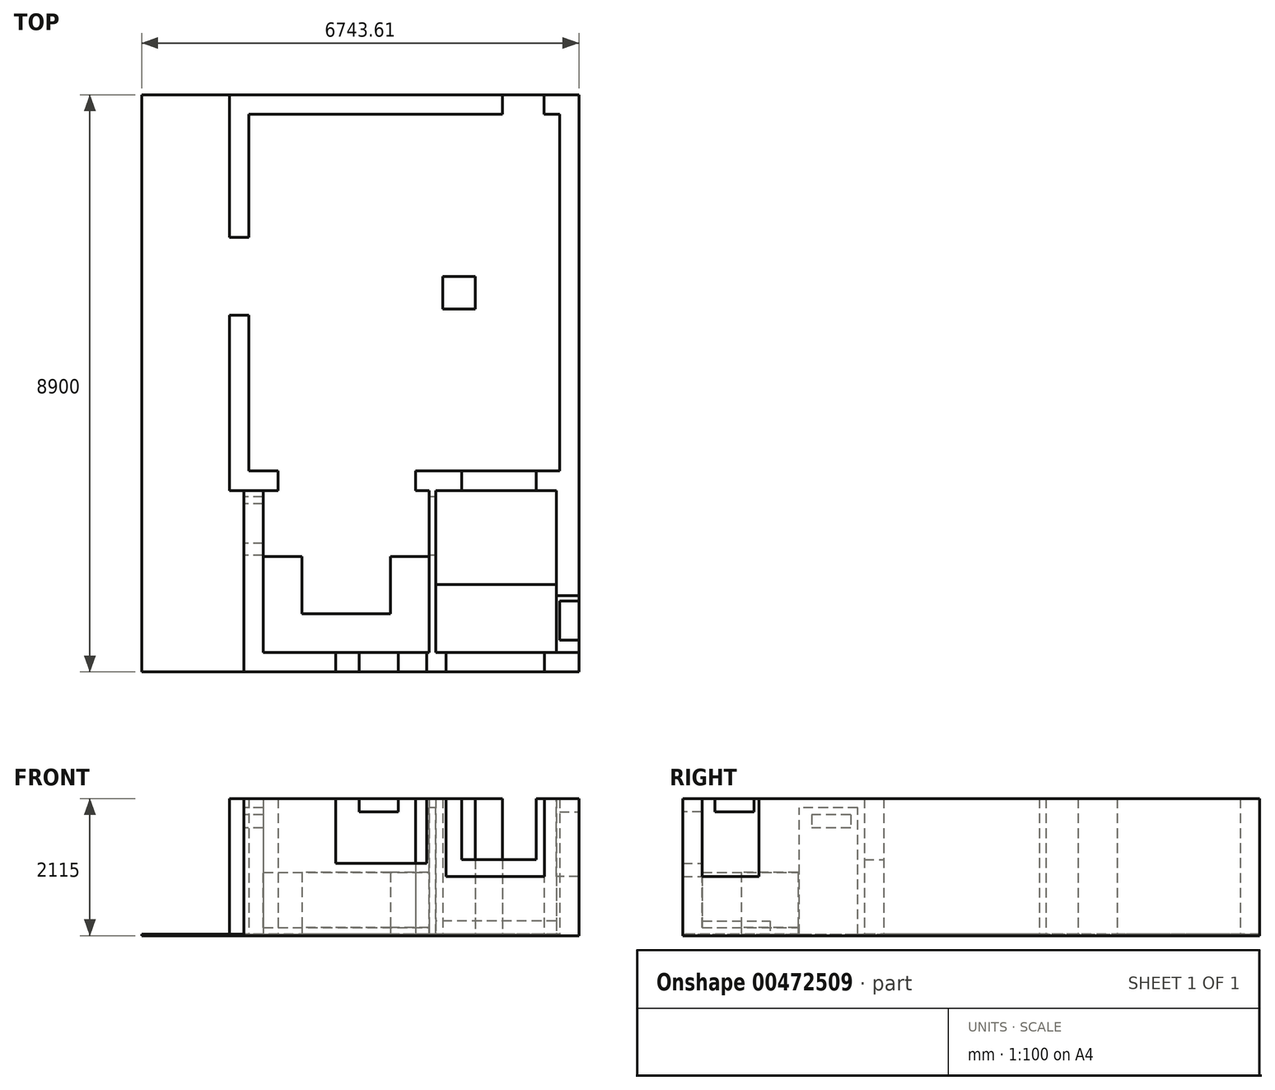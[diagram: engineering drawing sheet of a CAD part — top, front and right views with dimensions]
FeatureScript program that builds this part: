
annotation { "Feature Type Name" : "Feature", "Feature Type Description" : "" }
export const myFeature = defineFeature(function(context is Context, id is Id, definition is map)
    precondition{}
    {
        {
            var Q0;
            Q0=qCreatedBy(makeId("Top.planeOp"),FACE);
            var sketch = newSketch(context, id + "F0", { "sketchPlane" : qUnion([Q0])});
            skLineSegment(sketch, "E0", {"start": v(-2549.23, -2913.2) * mm, "end": v(-2549.23, -513.2) * mm});
            skLineSegment(sketch, "E1", {"start": v(-2549.23, -513.2) * mm, "end": v(-2549.23, 686.8) * mm});
            skLineSegment(sketch, "E2", {"start": v(-2549.23, 686.8) * mm, "end": v(-2549.23, 2586.8) * mm});
            skLineSegment(sketch, "E3", {"start": v(-2549.23, 2586.8) * mm, "end": v(1357.86, 2586.8) * mm});
            skLineSegment(sketch, "E4", {"start": v(1357.86, 2586.8) * mm, "end": v(1999.13, 2586.8) * mm});
            skLineSegment(sketch, "E5", {"start": v(1999.13, 2586.8) * mm, "end": v(2240.77, 2586.8) * mm});
            skLineSegment(sketch, "E6", {"start": v(2240.77, 2586.8) * mm, "end": v(2240.77, -2913.2) * mm});
            skLineSegment(sketch, "E7", {"start": v(2240.77, -2913.2) * mm, "end": v(1880.77, -2913.2) * mm});
            skLineSegment(sketch, "E8", {"start": v(1880.77, -2913.2) * mm, "end": v(730.77, -2913.2) * mm});
            skLineSegment(sketch, "E9", {"start": v(730.77, -2913.2) * mm, "end": v(20.77, -2913.2) * mm});
            skLineSegment(sketch, "E10", {"start": v(20.77, -2913.2) * mm, "end": v(-2099.23, -2913.2) * mm});
            skLineSegment(sketch, "E11", {"start": v(-2099.23, -2913.2) * mm, "end": v(-2549.23, -2913.2) * mm});
            skLineSegment(sketch, "E12", {"start": v(-2549.23, 686.8) * mm, "end": v(-2849.23, 686.8) * mm});
            skLineSegment(sketch, "E13", {"start": v(-2849.23, 686.8) * mm, "end": v(-2849.23, -513.2) * mm});
            skLineSegment(sketch, "E14", {"start": v(-2849.23, -513.2) * mm, "end": v(-2549.23, -513.2) * mm});
            skLineSegment(sketch, "E15", {"start": v(-2849.23, -513.2) * mm, "end": v(-2849.23, -3213.2) * mm});
            skLineSegment(sketch, "E16", {"start": v(-2849.23, -3213.2) * mm, "end": v(-2099.23, -3213.2) * mm});
            skLineSegment(sketch, "E17", {"start": v(-2099.23, -3213.2) * mm, "end": v(-2099.23, -2913.2) * mm});
            skLineSegment(sketch, "E18", {"start": v(-2099.23, -3213.2) * mm, "end": v(20.77, -3213.2) * mm});
            skLineSegment(sketch, "E19", {"start": v(20.77, -3213.2) * mm, "end": v(730.77, -3213.2) * mm});
            skLineSegment(sketch, "E20", {"start": v(730.77, -3213.2) * mm, "end": v(1880.77, -3213.2) * mm});
            skLineSegment(sketch, "E21", {"start": v(1880.77, -3213.2) * mm, "end": v(2190.77, -3213.2) * mm});
            skLineSegment(sketch, "E22", {"start": v(2540.77, -3213.2) * mm, "end": v(2540.77, 2886.8) * mm});
            skLineSegment(sketch, "E23", {"start": v(2540.77, 2886.8) * mm, "end": v(1999.13, 2886.8) * mm});
            skLineSegment(sketch, "E24", {"start": v(1999.13, 2886.8) * mm, "end": v(1357.86, 2886.8) * mm});
            skLineSegment(sketch, "E25", {"start": v(1357.86, 2886.8) * mm, "end": v(-2849.23, 2886.8) * mm});
            skLineSegment(sketch, "E26", {"start": v(-2849.23, 2886.8) * mm, "end": v(-2849.23, 686.8) * mm});
            skLineSegment(sketch, "E27", {"start": v(1357.86, 2586.8) * mm, "end": v(1357.86, 2886.8) * mm});
            skLineSegment(sketch, "E28", {"start": v(1999.13, 2586.8) * mm, "end": v(1999.13, 2886.8) * mm});
            skLineSegment(sketch, "E29", {"start": v(20.77, -3213.2) * mm, "end": v(20.77, -2913.2) * mm});
            skLineSegment(sketch, "E30", {"start": v(730.77, -3213.2) * mm, "end": v(730.77, -2913.2) * mm});
            skLineSegment(sketch, "E31", {"start": v(1880.77, -3213.2) * mm, "end": v(1880.77, -2913.2) * mm});
            skLineSegment(sketch, "E32.bottom", {"start": v(440.77, 86.8) * mm, "end": v(940.77, 86.8) * mm});
            skLineSegment(sketch, "E32.top", {"start": v(440.77, -413.2) * mm, "end": v(940.77, -413.2) * mm});
            skLineSegment(sketch, "E32.left", {"start": v(440.77, 86.8) * mm, "end": v(440.77, -413.2) * mm});
            skLineSegment(sketch, "E32.right", {"start": v(940.77, 86.8) * mm, "end": v(940.77, -413.2) * mm});
            skLineSegment(sketch, "E33", {"start": v(2540.77, -3213.2) * mm, "end": v(2540.77, -3423.2) * mm});
            skLineSegment(sketch, "E34", {"start": v(2540.77, -5713.2) * mm, "end": v(2310.77, -5713.2) * mm});
            skLineSegment(sketch, "E35", {"start": v(2190.77, -5713.2) * mm, "end": v(2190.77, -3213.2) * mm});
            skLineSegment(sketch, "E36", {"start": v(2190.77, -3213.2) * mm, "end": v(2190.77, -3213.2) * mm});
            skLineSegment(sketch, "E37", {"start": v(2190.77, -3213.2) * mm, "end": v(2540.77, -3213.2) * mm});
            skLineSegment(sketch, "E38", {"start": v(2540.77, -3423.2) * mm, "end": v(2540.77, -4153.2) * mm});
            skLineSegment(sketch, "E39", {"start": v(2540.77, -4153.2) * mm, "end": v(2540.77, -4593.2) * mm});
            skLineSegment(sketch, "E40", {"start": v(2540.77, -4593.2) * mm, "end": v(2540.77, -4833.2) * mm});
            skLineSegment(sketch, "E41", {"start": v(2540.77, -4833.2) * mm, "end": v(2540.77, -5023.2) * mm});
            skLineSegment(sketch, "E42", {"start": v(2540.77, -5023.2) * mm, "end": v(2540.77, -5713.2) * mm});
            skLineSegment(sketch, "E43", {"start": v(2540.77, -3423.2) * mm, "end": v(2190.77, -3423.2) * mm});
            skLineSegment(sketch, "E44", {"start": v(2540.77, -4153.2) * mm, "end": v(2190.77, -4153.2) * mm});
            skLineSegment(sketch, "E45", {"start": v(2540.77, -4593.2) * mm, "end": v(2190.77, -4593.2) * mm});
            skLineSegment(sketch, "E46", {"start": v(2540.77, -4833.2) * mm, "end": v(2190.77, -4833.2) * mm});
            skLineSegment(sketch, "E47", {"start": v(2540.77, -5023.2) * mm, "end": v(2190.77, -5023.2) * mm});
            skLineSegment(sketch, "E48", {"start": v(2310.77, -5713.2) * mm, "end": v(2190.77, -5713.2) * mm});
            skLineSegment(sketch, "E49", {"start": v(2190.77, -5713.2) * mm, "end": v(2010.77, -5713.2) * mm});
            skLineSegment(sketch, "E50", {"start": v(2010.77, -5713.2) * mm, "end": v(2010.77, -6013.2) * mm});
            skLineSegment(sketch, "E51", {"start": v(2010.77, -6013.2) * mm, "end": v(2310.77, -6013.2) * mm});
            skLineSegment(sketch, "E52", {"start": v(2310.77, -6013.2) * mm, "end": v(2310.77, -5713.2) * mm});
            skLineSegment(sketch, "E53", {"start": v(2010.77, -6013.2) * mm, "end": v(490.77, -6013.2) * mm, "construction": true});
            skLineSegment(sketch, "E54", {"start": v(490.77, -6013.2) * mm, "end": v(190.77, -6013.2) * mm});
            skLineSegment(sketch, "E55", {"start": v(190.77, -6013.2) * mm, "end": v(-2329.23, -6013.2) * mm, "construction": true});
            skLineSegment(sketch, "E56", {"start": v(-2329.23, -6013.2) * mm, "end": v(-2629.23, -6013.2) * mm});
            skLineSegment(sketch, "E57", {"start": v(2010.77, -5713.2) * mm, "end": v(490.77, -5713.2) * mm, "construction": true});
            skLineSegment(sketch, "E58", {"start": v(490.77, -5713.2) * mm, "end": v(190.77, -5713.2) * mm});
            skLineSegment(sketch, "E59", {"start": v(190.77, -5713.2) * mm, "end": v(-2329.23, -5713.2) * mm, "construction": true});
            skLineSegment(sketch, "E60", {"start": v(-2329.23, -5713.2) * mm, "end": v(-2629.23, -5713.2) * mm});
            skLineSegment(sketch, "E61", {"start": v(-2629.23, -5713.2) * mm, "end": v(-2629.23, -6013.2) * mm});
            skLineSegment(sketch, "E62", {"start": v(-2329.23, -6013.2) * mm, "end": v(-2329.23, -5713.2) * mm});
            skLineSegment(sketch, "E63", {"start": v(190.77, -6013.2) * mm, "end": v(190.77, -5713.2) * mm});
            skLineSegment(sketch, "E64", {"start": v(490.77, -6013.2) * mm, "end": v(490.77, -5713.2) * mm});
            skLineSegment(sketch, "E65", {"start": v(-2629.23, -5713.2) * mm, "end": v(-2629.23, -3213.2) * mm, "construction": true});
            skSolve(sketch);
        }
        {
            var Q0;
            Q0=makeQuery(id+"F0.imprint","IMPRINT",FACE,{"disambiguationData":[TD([[makeQuery(id+"F0.imprint","IMPRINT",EDGE,{"derivedFrom":sQuery(id+"F0.wireOp",EDGE,"E33")}),-1.0]])]});
            extrude(context, id + "F1", {"entities" : qUnion([Q0]), "depth" : 1610 * mm, "offsetDistance" : 25 * mm});
        }
        {
            var Q0;
            Q0=makeQuery(id+"F0.imprint","IMPRINT",FACE,{"disambiguationData":[TD([[makeQuery(id+"F0.imprint","IMPRINT",EDGE,{"derivedFrom":sQuery(id+"F0.wireOp",EDGE,"E38")}),-1.0]])]});
            extrude(context, id + "F2", {"entities" : qUnion([Q0]), "operationType" : NewBodyOperationType.ADD, "depth" : 1400 * mm, "offsetDistance" : 25 * mm});
        }
        {
            var Q0;
            Q0=makeQuery(id+"F0.imprint","IMPRINT",FACE,{"disambiguationData":[TD([[makeQuery(id+"F0.imprint","IMPRINT",EDGE,{"derivedFrom":sQuery(id+"F0.wireOp",EDGE,"E39")}),-1.0]])]});
            extrude(context, id + "F3", {"entities" : qUnion([Q0]), "operationType" : NewBodyOperationType.ADD, "depth" : 1170 * mm, "offsetDistance" : 25 * mm});
        }
        {
            var Q0;
            Q0=makeQuery(id+"F0.imprint","IMPRINT",FACE,{"disambiguationData":[TD([[makeQuery(id+"F0.imprint","IMPRINT",EDGE,{"derivedFrom":sQuery(id+"F0.wireOp",EDGE,"E40")}),-1.0]])]});
            extrude(context, id + "F4", {"entities" : qUnion([Q0]), "operationType" : NewBodyOperationType.ADD, "depth" : 1020 * mm, "offsetDistance" : 25 * mm});
        }
        {
            var Q0;
            Q0=makeQuery(id+"F0.imprint","IMPRINT",FACE,{"disambiguationData":[TD([[makeQuery(id+"F0.imprint","IMPRINT",EDGE,{"derivedFrom":sQuery(id+"F0.wireOp",EDGE,"E41")}),-1.0]])]});
            extrude(context, id + "F5", {"entities" : qUnion([Q0]), "operationType" : NewBodyOperationType.ADD, "depth" : 660 * mm, "offsetDistance" : 25 * mm});
        }
        {
            var Q0;
            Q0=makeQuery(id+"F0.imprint","IMPRINT",FACE,{"disambiguationData":[TD([[makeQuery(id+"F0.imprint","IMPRINT",EDGE,{"derivedFrom":sQuery(id+"F0.wireOp",EDGE,"E34")}),-1.0]])]});
            extrude(context, id + "F6", {"entities" : qUnion([Q0]), "operationType" : NewBodyOperationType.ADD, "depth" : 470 * mm, "offsetDistance" : 25 * mm});
        }
        {
            var Q0;
            Q0=makeQuery(id+"F0.imprint","IMPRINT",FACE,{"disambiguationData":[TD([[makeQuery(id+"F0.imprint","IMPRINT",EDGE,{"derivedFrom":sQuery(id+"F0.wireOp",EDGE,"E56")}),-1.0]])]});
            var Q1;
            Q1=makeQuery(id+"F0.imprint","IMPRINT",FACE,{"disambiguationData":[TD([[makeQuery(id+"F0.imprint","IMPRINT",EDGE,{"derivedFrom":sQuery(id+"F0.wireOp",EDGE,"E54")}),-1.0]])]});
            var Q2;
            Q2=makeQuery(id+"F0.imprint","IMPRINT",FACE,{"disambiguationData":[TD([[makeQuery(id+"F0.imprint","IMPRINT",EDGE,{"derivedFrom":sQuery(id+"F0.wireOp",EDGE,"E48")}),1.0]])]});
            extrude(context, id + "F7", {"entities" : qUnion([Q0, Q1, Q2]), "operationType" : NewBodyOperationType.ADD, "depth" : 2090 * mm, "offsetDistance" : 25 * mm});
        }
        {
            var Q0;
            Q0=makeQuery(id+"F0.imprint","IMPRINT",FACE,{"disambiguationData":[TD([[makeQuery(id+"F0.imprint","IMPRINT",EDGE,{"derivedFrom":sQuery(id+"F0.wireOp",EDGE,"E2")}),1.0]])]});
            var Q1;
            Q1=makeQuery(id+"F0.imprint","IMPRINT",FACE,{"disambiguationData":[TD([[makeQuery(id+"F0.imprint","IMPRINT",EDGE,{"derivedFrom":sQuery(id+"F0.wireOp",EDGE,"E32.bottom")}),-1.0]])]});
            var Q2;
            Q2=makeQuery(id+"F0.imprint","IMPRINT",FACE,{"disambiguationData":[TD([[makeQuery(id+"F0.imprint","IMPRINT",EDGE,{"derivedFrom":sQuery(id+"F0.wireOp",EDGE,"E0")}),1.0]])]});
            var Q3;
            Q3=makeQuery(id+"F0.imprint","IMPRINT",FACE,{"disambiguationData":[TD([[makeQuery(id+"F0.imprint","IMPRINT",EDGE,{"derivedFrom":sQuery(id+"F0.wireOp",EDGE,"E9")}),1.0]])]});
            var Q4;
            Q4=makeQuery(id+"F0.imprint","IMPRINT",FACE,{"disambiguationData":[TD([[makeQuery(id+"F0.imprint","IMPRINT",EDGE,{"derivedFrom":sQuery(id+"F0.wireOp",EDGE,"E5")}),1.0]])]});
            extrude(context, id + "F8", {"entities" : qUnion([Q0, Q1, Q2, Q3, Q4]), "operationType" : NewBodyOperationType.ADD, "depth" : 2090 * mm, "offsetDistance" : 25 * mm});
        }
        {
            var Q0;
            Q0=makeQuery(id+"F8.opExtrude","CAP_FACE",FACE,{"disambiguationData":[OSD([sQuery(id+"F0.wireOp",EDGE,"E2"),sQuery(id+"F0.wireOp",EDGE,"E3"),sQuery(id+"F0.wireOp",EDGE,"E12"),sQuery(id+"F0.wireOp",EDGE,"E25"),sQuery(id+"F0.wireOp",EDGE,"E26"),sQuery(id+"F0.wireOp",EDGE,"E27")])],"isStart":true});
            var sketch = newSketch(context, id + "F9", { "sketchPlane" : qUnion([Q0])});
            skLineSegment(sketch, "E66.bottom", {"start": v(-2849.23, -2886.8) * mm, "end": v(2540.77, -2886.8) * mm});
            skLineSegment(sketch, "E66.top", {"start": v(-2849.23, 6013.2) * mm, "end": v(2540.77, 6013.2) * mm});
            skLineSegment(sketch, "E66.left", {"start": v(-2849.23, -2886.8) * mm, "end": v(-2849.23, 6013.2) * mm, "construction": true});
            skLineSegment(sketch, "E66.right", {"start": v(2540.77, -2886.8) * mm, "end": v(2540.77, 6013.2) * mm});
            skLineSegment(sketch, "E67", {"start": v(-2849.23, 6013.2) * mm, "end": v(-4202.84, 6013.2) * mm});
            skLineSegment(sketch, "E68", {"start": v(-4202.84, 6013.2) * mm, "end": v(-4202.84, -2886.8) * mm});
            skLineSegment(sketch, "E69", {"start": v(-4202.84, -2886.8) * mm, "end": v(-2849.23, -2886.8) * mm});
            skSolve(sketch);
        }
        {
            var Q0;
            {var subQ3=sQuery(id+"F9.wireOp",EDGE,"E66.top");Q0=makeQuery(id+"F9.imprint","IMPRINT",FACE,{"disambiguationData":[TD([[makeQuery(id+"F9.imprint","IMPRINT",EDGE,{"derivedFrom":subQ3}),-1.0]])]});}
            var Q1;
            Q1=makeQuery(id+"F9.imprint","IMPRINT",FACE,{"disambiguationData":[TD([[makeQuery(id+"F9.imprint","IMPRINT",EDGE,{"derivedFrom":makeQuery(id+"F8.opExtrude","CAP_EDGE",EDGE,{"disambiguationData":[OSD([sQuery(id+"F0.wireOp",EDGE,"E2")])],"isStart":true})}),-1.0]])]});
            extrude(context, id + "F10", {"entities" : qUnion([Q0, Q1]), "depth" : 25 * mm, "offsetDistance" : 25 * mm});
        }
        {
            var Q0;
            Q0=makeQuery(id+"F10.opExtrude","CAP_FACE",FACE,{"disambiguationData":[OSD([sQuery(id+"F9.wireOp",EDGE,"E66.bottom"),sQuery(id+"F9.wireOp",EDGE,"E66.top"),sQuery(id+"F9.wireOp",EDGE,"E66.left"),sQuery(id+"F9.wireOp",EDGE,"E66.right")])],"isStart":true});
            var sketch = newSketch(context, id + "F11", { "sketchPlane" : qUnion([Q0])});
            skLineSegment(sketch, "E70.bottom", {"start": v(730.77, -3213.2) * mm, "end": v(1880.77, -3213.2) * mm});
            skLineSegment(sketch, "E70.top", {"start": v(730.77, -2913.2) * mm, "end": v(1880.77, -2913.2) * mm});
            skLineSegment(sketch, "E70.left", {"start": v(730.77, -3213.2) * mm, "end": v(730.77, -2913.2) * mm});
            skLineSegment(sketch, "E70.right", {"start": v(1880.77, -3213.2) * mm, "end": v(1880.77, -2913.2) * mm});
            skSolve(sketch);
        }
        {
            var Q0;
            Q0=makeQuery(id+"F11.imprint","IMPRINT",FACE,{"disambiguationData":[TD([[makeQuery(id+"F11.imprint","IMPRINT",EDGE,{"derivedFrom":sQuery(id+"F11.wireOp",EDGE,"E70.bottom")}),1.0]])]});
            extrude(context, id + "F12", {"entities" : qUnion([Q0]), "operationType" : NewBodyOperationType.ADD, "depth" : 1150 * mm, "offsetDistance" : 25 * mm});
        }
        {
            var Q0;
            {var subQ0=sQuery(id+"F9.wireOp",EDGE,"E68");var subQ1=sQuery(id+"F9.wireOp",EDGE,"E67");var subQ2=sQuery(id+"F9.wireOp",EDGE,"E66.top");var subQ3=sQuery(id+"F0.wireOp",EDGE,"E35");var subQ4=sQuery(id+"F9.wireOp",EDGE,"E69");var subQ5=sQuery(id+"F9.wireOp",EDGE,"E66.bottom");Q0=makeQuery(id+"F12.boolean.opBoolean","SPLIT",FACE,{"disambiguationData":[TD([makeQuery(id+"F1.opExtrude","SWEPT_FACE",FACE,{"disambiguationData":[OSD([subQ3])]})])],"derivedFrom":makeQuery(id+"F10.opExtrude","CAP_FACE",FACE,{"disambiguationData":[OSD([subQ5,subQ2,sQuery(id+"F9.wireOp",EDGE,"E66.right"),subQ1,subQ0,subQ4])],"isStart":true})});}
            var sketch = newSketch(context, id + "F13", { "sketchPlane" : qUnion([Q0])});
            skLineSegment(sketch, "E71.bottom", {"start": v(-5304.36, -2795.92) * mm, "end": v(3545.4, -2795.92) * mm});
            skLineSegment(sketch, "E71.top", {"start": v(-5304.36, 3060.85) * mm, "end": v(3545.4, 3060.85) * mm});
            skLineSegment(sketch, "E71.left", {"start": v(-5304.36, -2795.92) * mm, "end": v(-5304.36, 3060.85) * mm});
            skLineSegment(sketch, "E71.right", {"start": v(3545.4, -2795.92) * mm, "end": v(3545.4, 3060.85) * mm});
            skSolve(sketch);
        }
        {
            var Q0;
            {var subQ0=sQuery(id+"F9.wireOp",EDGE,"E68");var subQ1=sQuery(id+"F9.wireOp",EDGE,"E67");var subQ2=sQuery(id+"F9.wireOp",EDGE,"E66.top");var subQ3=sQuery(id+"F0.wireOp",EDGE,"E35");var subQ4=sQuery(id+"F9.wireOp",EDGE,"E69");var subQ5=sQuery(id+"F9.wireOp",EDGE,"E66.bottom");Q0=makeQuery(id+"F12.boolean.opBoolean","SPLIT",FACE,{"disambiguationData":[TD([makeQuery(id+"F1.opExtrude","SWEPT_FACE",FACE,{"disambiguationData":[OSD([subQ3])]})])],"derivedFrom":makeQuery(id+"F10.opExtrude","CAP_FACE",FACE,{"disambiguationData":[OSD([subQ5,subQ2,sQuery(id+"F9.wireOp",EDGE,"E66.right"),subQ1,subQ0,subQ4])],"isStart":true})});}
            var sketch = newSketch(context, id + "F14", { "sketchPlane" : qUnion([Q0])});
            skLineSegment(sketch, "E72.bottom", {"start": v(-2629.23, -5713.2) * mm, "end": v(-2329.23, -5713.2) * mm});
            skLineSegment(sketch, "E72.top", {"start": v(-2629.23, -3213.2) * mm, "end": v(-2329.23, -3213.2) * mm});
            skLineSegment(sketch, "E72.left", {"start": v(-2629.23, -5713.2) * mm, "end": v(-2629.23, -3213.2) * mm});
            skLineSegment(sketch, "E72.right", {"start": v(-2329.23, -5713.2) * mm, "end": v(-2329.23, -3213.2) * mm});
            skLineSegment(sketch, "E73.bottom", {"start": v(-2329.23, -5713.2) * mm, "end": v(190.77, -5713.2) * mm});
            skLineSegment(sketch, "E73.top", {"start": v(-2329.23, -6013.2) * mm, "end": v(190.77, -6013.2) * mm});
            skLineSegment(sketch, "E73.left", {"start": v(-2329.23, -5713.2) * mm, "end": v(-2329.23, -6013.2) * mm});
            skLineSegment(sketch, "E73.right", {"start": v(190.77, -5713.2) * mm, "end": v(190.77, -6013.2) * mm});
            skLineSegment(sketch, "E74.bottom", {"start": v(2010.77, -5713.2) * mm, "end": v(490.77, -5713.2) * mm});
            skLineSegment(sketch, "E74.top", {"start": v(2010.77, -6013.2) * mm, "end": v(490.77, -6013.2) * mm});
            skLineSegment(sketch, "E74.left", {"start": v(2010.77, -5713.2) * mm, "end": v(2010.77, -6013.2) * mm});
            skLineSegment(sketch, "E74.right", {"start": v(490.77, -5713.2) * mm, "end": v(490.77, -6013.2) * mm});
            skLineSegment(sketch, "E75.bottom", {"start": v(2310.77, -6013.2) * mm, "end": v(2540.77, -6013.2) * mm});
            skLineSegment(sketch, "E75.top", {"start": v(2310.77, -5713.2) * mm, "end": v(2540.77, -5713.2) * mm});
            skLineSegment(sketch, "E75.left", {"start": v(2310.77, -6013.2) * mm, "end": v(2310.77, -5713.2) * mm});
            skLineSegment(sketch, "E75.right", {"start": v(2540.77, -6013.2) * mm, "end": v(2540.77, -5713.2) * mm});
            skLineSegment(sketch, "E76", {"start": v(230.77, -5713.2) * mm, "end": v(230.77, -3213.2) * mm});
            skLineSegment(sketch, "E77", {"start": v(230.77, -3213.2) * mm, "end": v(330.77, -3213.2) * mm});
            skLineSegment(sketch, "E78", {"start": v(330.77, -3213.2) * mm, "end": v(330.77, -5713.2) * mm});
            skLineSegment(sketch, "E79", {"start": v(330.77, -5713.2) * mm, "end": v(230.77, -5713.2) * mm});
            skSolve(sketch);
        }
        {
            var Q0;
            Q0 = qSketchRegion(id + "F14", true);
            var Q1;
            Q1=makeQuery(id+"F8.opExtrude","CAP_FACE",FACE,{"disambiguationData":[OSD([sQuery(id+"F0.wireOp",EDGE,"E0"),sQuery(id+"F0.wireOp",EDGE,"E11"),sQuery(id+"F0.wireOp",EDGE,"E14"),sQuery(id+"F0.wireOp",EDGE,"E15"),sQuery(id+"F0.wireOp",EDGE,"E16"),sQuery(id+"F0.wireOp",EDGE,"E17")])],"isStart":false});
            extrude(context, id + "F15", {"entities" : qUnion([Q0]), "endBound" : BoundingType.UP_TO_SURFACE, "depth" : 25 * mm, "endBoundEntityFace" : qUnion([Q1]), "offsetDistance" : 25 * mm});
        }
        {
            var Q0;
            Q0=makeQuery(id+"F12.boolean.opBoolean","MERGE",FACE,{"derivedFrom":[makeQuery(id+"F8.boolean.opBoolean","MERGE",FACE,{"derivedFrom":[makeQuery(id+"F6.boolean.opBoolean","MERGE",FACE,{"derivedFrom":[makeQuery(id+"F5.boolean.opBoolean","MERGE",FACE,{"derivedFrom":[makeQuery(id+"F4.boolean.opBoolean","MERGE",FACE,{"derivedFrom":[makeQuery(id+"F3.boolean.opBoolean","MERGE",FACE,{"derivedFrom":[makeQuery(id+"F2.boolean.opBoolean","MERGE",FACE,{"derivedFrom":[makeQuery(id+"F1.opExtrude","SWEPT_FACE",FACE,{"disambiguationData":[OSD([sQuery(id+"F0.wireOp",EDGE,"E33")])]}),makeQuery(id+"F2.opExtrude","SWEPT_FACE",FACE,{"disambiguationData":[OSD([sQuery(id+"F0.wireOp",EDGE,"E38")])]})]}),makeQuery(id+"F3.opExtrude","SWEPT_FACE",FACE,{"disambiguationData":[OSD([sQuery(id+"F0.wireOp",EDGE,"E39")])]})]}),makeQuery(id+"F4.opExtrude","SWEPT_FACE",FACE,{"disambiguationData":[OSD([sQuery(id+"F0.wireOp",EDGE,"E40")])]})]}),makeQuery(id+"F5.opExtrude","SWEPT_FACE",FACE,{"disambiguationData":[OSD([sQuery(id+"F0.wireOp",EDGE,"E41")])]})]}),makeQuery(id+"F6.opExtrude","SWEPT_FACE",FACE,{"disambiguationData":[OSD([sQuery(id+"F0.wireOp",EDGE,"E42")])]})]}),makeQuery(id+"F8.opExtrude","SWEPT_FACE",FACE,{"disambiguationData":[OSD([sQuery(id+"F0.wireOp",EDGE,"E22")])]})]}),makeQuery(id+"F10.opExtrude","SWEPT_FACE",FACE,{"disambiguationData":[OSD([sQuery(id+"F9.wireOp",EDGE,"E66.right")])]})]});
            var sketch = newSketch(context, id + "F16", { "sketchPlane" : qUnion([Q0])});
            skLineSegment(sketch, "E80", {"start": v(-5713.2, 470) * mm, "end": v(-5023.2, 470) * mm});
            skLineSegment(sketch, "E81", {"start": v(-5023.2, 470) * mm, "end": v(-5023.2, 660) * mm});
            skLineSegment(sketch, "E82", {"start": v(-5023.2, 660) * mm, "end": v(-4833.2, 660) * mm});
            skLineSegment(sketch, "E83", {"start": v(-4833.2, 660) * mm, "end": v(-4833.2, 1020) * mm});
            skLineSegment(sketch, "E84", {"start": v(-4833.2, 1020) * mm, "end": v(-4593.2, 1020) * mm});
            skLineSegment(sketch, "E85", {"start": v(-4593.2, 1020) * mm, "end": v(-4593.2, 1170) * mm});
            skLineSegment(sketch, "E86", {"start": v(-4593.2, 1170) * mm, "end": v(-4153.2, 1170) * mm});
            skLineSegment(sketch, "E87", {"start": v(-4153.2, 1170) * mm, "end": v(-4153.2, 1400) * mm});
            skLineSegment(sketch, "E88", {"start": v(-4153.2, 1400) * mm, "end": v(-3423.2, 1400) * mm});
            skLineSegment(sketch, "E89", {"start": v(-3423.2, 1400) * mm, "end": v(-3423.2, 1610) * mm});
            skLineSegment(sketch, "E90", {"start": v(-3423.2, 1610) * mm, "end": v(-3213.2, 1610) * mm});
            skLineSegment(sketch, "E91", {"start": v(-3213.2, 1610) * mm, "end": v(-3213.2, 2090) * mm});
            skLineSegment(sketch, "E92", {"start": v(-3213.2, 2090) * mm, "end": v(-5713.2, 2090) * mm});
            skLineSegment(sketch, "E93", {"start": v(-5713.2, 2090) * mm, "end": v(-5713.2, 470) * mm});
            skSolve(sketch);
        }
        {
            var Q0;
            Q0 = qSketchRegion(id + "F16", true);
            var Q1;
            {var subQ0=sQuery(id+"F0.wireOp",EDGE,"E35");Q1=makeQuery(id+"F6.boolean.opBoolean","MERGE",FACE,{"derivedFrom":[makeQuery(id+"F5.boolean.opBoolean","MERGE",FACE,{"derivedFrom":[makeQuery(id+"F4.boolean.opBoolean","MERGE",FACE,{"derivedFrom":[makeQuery(id+"F3.boolean.opBoolean","MERGE",FACE,{"derivedFrom":[makeQuery(id+"F2.boolean.opBoolean","MERGE",FACE,{"derivedFrom":[makeQuery(id+"F1.opExtrude","SWEPT_FACE",FACE,{"disambiguationData":[OSD([subQ0])]}),makeQuery(id+"F2.opExtrude","SWEPT_FACE",FACE,{"disambiguationData":[OSD([subQ0])]})]}),makeQuery(id+"F3.opExtrude","SWEPT_FACE",FACE,{"disambiguationData":[OSD([subQ0])]})]}),makeQuery(id+"F4.opExtrude","SWEPT_FACE",FACE,{"disambiguationData":[OSD([subQ0])]})]}),makeQuery(id+"F5.opExtrude","SWEPT_FACE",FACE,{"disambiguationData":[OSD([subQ0])]})]}),makeQuery(id+"F6.opExtrude","SWEPT_FACE",FACE,{"disambiguationData":[OSD([subQ0])]})]});}
            extrude(context, id + "F17", {"entities" : qUnion([Q0]), "operationType" : NewBodyOperationType.ADD, "endBound" : BoundingType.UP_TO_SURFACE, "oppositeDirection" : true, "depth" : 300 * mm, "endBoundEntityFace" : qUnion([Q1]), "offsetDistance" : 25 * mm});
        }
        {
            var Q0;
            Q0=makeQuery(id+"F15.opExtrude","SWEPT_FACE",FACE,{"disambiguationData":[OSD([sQuery(id+"F14.wireOp",EDGE,"E73.bottom")])]});
            var sketch = newSketch(context, id + "F18", { "sketchPlane" : qUnion([Q0])});
            skLineSegment(sketch, "E94.bottom", {"start": v(-190.77, 1090) * mm, "end": v(1209.23, 1090) * mm});
            skLineSegment(sketch, "E94.top", {"start": v(-190.77, 2090) * mm, "end": v(1209.23, 2090) * mm});
            skLineSegment(sketch, "E94.left", {"start": v(-190.77, 1090) * mm, "end": v(-190.77, 2090) * mm});
            skLineSegment(sketch, "E94.right", {"start": v(1209.23, 1090) * mm, "end": v(1209.23, 2090) * mm});
            skLineSegment(sketch, "E95.bottom", {"start": v(-2010.77, 2090) * mm, "end": v(-490.77, 2090) * mm});
            skLineSegment(sketch, "E95.top", {"start": v(-2010.77, 890) * mm, "end": v(-490.77, 890) * mm});
            skLineSegment(sketch, "E95.left", {"start": v(-2010.77, 2090) * mm, "end": v(-2010.77, 890) * mm});
            skLineSegment(sketch, "E95.right", {"start": v(-490.77, 2090) * mm, "end": v(-490.77, 890) * mm});
            skSolve(sketch);
        }
        {
            var Q0;
            Q0=makeQuery(id+"F18.imprint","IMPRINT",FACE,{"disambiguationData":[TD([[makeQuery(id+"F18.imprint","IMPRINT",EDGE,{"derivedFrom":sQuery(id+"F18.wireOp",EDGE,"E94.bottom")}),1.0]])]});
            var Q1;
            Q1=makeQuery(id+"F18.imprint","IMPRINT",FACE,{"disambiguationData":[TD([[makeQuery(id+"F18.imprint","IMPRINT",EDGE,{"derivedFrom":sQuery(id+"F18.wireOp",EDGE,"E95.bottom")}),-1.0]])]});
            extrude(context, id + "F19", {"entities" : qUnion([Q0, Q1]), "operationType" : NewBodyOperationType.REMOVE, "endBound" : BoundingType.UP_TO_NEXT, "oppositeDirection" : true, "depth" : 25 * mm, "offsetDistance" : 25 * mm});
        }
        {
            var Q0;
            Q0=makeQuery(id+"F17.opExtrude","CAP_FACE",FACE,{"disambiguationData":[OSD([sQuery(id+"F16.wireOp",EDGE,"E80"),sQuery(id+"F16.wireOp",EDGE,"E81"),sQuery(id+"F16.wireOp",EDGE,"E82"),sQuery(id+"F16.wireOp",EDGE,"E83"),sQuery(id+"F16.wireOp",EDGE,"E84"),sQuery(id+"F16.wireOp",EDGE,"E85"),sQuery(id+"F16.wireOp",EDGE,"E86"),sQuery(id+"F16.wireOp",EDGE,"E87"),sQuery(id+"F16.wireOp",EDGE,"E88"),sQuery(id+"F16.wireOp",EDGE,"E89"),sQuery(id+"F16.wireOp",EDGE,"E90"),sQuery(id+"F16.wireOp",EDGE,"E91"),sQuery(id+"F16.wireOp",EDGE,"E92"),sQuery(id+"F16.wireOp",EDGE,"E93")])],"isStart":false});
            var sketch = newSketch(context, id + "F20", { "sketchPlane" : qUnion([Q0])});
            skLineSegment(sketch, "E96.bottom", {"start": v(5713.2, 890) * mm, "end": v(4833.2, 890) * mm});
            skLineSegment(sketch, "E96.top", {"start": v(5713.2, 2090) * mm, "end": v(4834.2, 2090) * mm});
            skLineSegment(sketch, "E96.left", {"start": v(5713.2, 890) * mm, "end": v(5713.2, 2090) * mm});
            skLineSegment(sketch, "E96.right", {"start": v(4834.2, 890) * mm, "end": v(4834.2, 2090) * mm});
            skSolve(sketch);
        }
        {
            var Q0;
            Q0 = qSketchRegion(id + "F20", true);
            extrude(context, id + "F21", {"entities" : qUnion([Q0]), "operationType" : NewBodyOperationType.REMOVE, "endBound" : BoundingType.UP_TO_NEXT, "oppositeDirection" : true, "depth" : 25 * mm, "offsetDistance" : 25 * mm});
        }
        {
            var Q0;
            Q0=makeQuery(id+"F15.opExtrude","SWEPT_FACE",FACE,{"disambiguationData":[OSD([sQuery(id+"F14.wireOp",EDGE,"E72.left")])]});
            var sketch = newSketch(context, id + "F22", { "sketchPlane" : qUnion([Q0])});
            skLineSegment(sketch, "E97.bottom", {"start": v(3313.2, 0) * mm, "end": v(4213.2, 0) * mm});
            skLineSegment(sketch, "E97.top", {"start": v(3313.2, 1950) * mm, "end": v(4213.2, 1950) * mm});
            skLineSegment(sketch, "E97.left", {"start": v(3313.2, 0) * mm, "end": v(3313.2, 1950) * mm});
            skLineSegment(sketch, "E97.right", {"start": v(4213.2, 0) * mm, "end": v(4213.2, 1950) * mm});
            skSolve(sketch);
        }
        {
            var Q0;
            Q0=makeQuery(id+"F22.imprint","IMPRINT",FACE,{"disambiguationData":[TD([[makeQuery(id+"F22.imprint","IMPRINT",EDGE,{"derivedFrom":sQuery(id+"F22.wireOp",EDGE,"E97.bottom")}),-1.0]])]});
            extrude(context, id + "F23", {"entities" : qUnion([Q0]), "operationType" : NewBodyOperationType.REMOVE, "endBound" : BoundingType.UP_TO_NEXT, "oppositeDirection" : true, "depth" : 25 * mm, "offsetDistance" : 25 * mm});
        }
        {
            var Q0;
            Q0=makeQuery(id+"F15.opExtrude","SWEPT_FACE",FACE,{"disambiguationData":[OSD([sQuery(id+"F14.wireOp",EDGE,"E76")])]});
            var sketch = newSketch(context, id + "F24", { "sketchPlane" : qUnion([Q0])});
            skLineSegment(sketch, "E98.bottom", {"start": v(3313.2, 0) * mm, "end": v(4213.2, 0) * mm});
            skLineSegment(sketch, "E98.top", {"start": v(3313.2, 1950) * mm, "end": v(4213.2, 1950) * mm});
            skLineSegment(sketch, "E98.left", {"start": v(3313.2, 0) * mm, "end": v(3313.2, 1950) * mm});
            skLineSegment(sketch, "E98.right", {"start": v(4213.2, 0) * mm, "end": v(4213.2, 1950) * mm});
            skSolve(sketch);
        }
        {
            var Q0;
            Q0=makeQuery(id+"F24.imprint","IMPRINT",FACE,{"disambiguationData":[TD([[makeQuery(id+"F24.imprint","IMPRINT",EDGE,{"derivedFrom":sQuery(id+"F24.wireOp",EDGE,"E98.bottom")}),-1.0]])]});
            extrude(context, id + "F25", {"entities" : qUnion([Q0]), "operationType" : NewBodyOperationType.REMOVE, "endBound" : BoundingType.UP_TO_NEXT, "oppositeDirection" : true, "depth" : 25 * mm, "offsetDistance" : 25 * mm});
        }
        {
            var Q0;
            {var subQ0=sQuery(id+"F9.wireOp",EDGE,"E68");var subQ1=sQuery(id+"F9.wireOp",EDGE,"E67");var subQ2=sQuery(id+"F9.wireOp",EDGE,"E66.top");var subQ3=sQuery(id+"F0.wireOp",EDGE,"E35");var subQ4=sQuery(id+"F9.wireOp",EDGE,"E69");var subQ5=sQuery(id+"F9.wireOp",EDGE,"E66.bottom");Q0=makeQuery(id+"F12.boolean.opBoolean","SPLIT",FACE,{"disambiguationData":[TD([makeQuery(id+"F1.opExtrude","SWEPT_FACE",FACE,{"disambiguationData":[OSD([subQ3])]})])],"derivedFrom":makeQuery(id+"F10.opExtrude","CAP_FACE",FACE,{"disambiguationData":[OSD([subQ5,subQ2,sQuery(id+"F9.wireOp",EDGE,"E66.right"),subQ1,subQ0,subQ4])],"isStart":true})});}
            var sketch = newSketch(context, id + "F26", { "sketchPlane" : qUnion([Q0])});
            skLineSegment(sketch, "E99.bottom", {"start": v(2190.77, -4663.2) * mm, "end": v(330.77, -4663.2) * mm});
            skLineSegment(sketch, "E99.top", {"start": v(2190.77, -5713.2) * mm, "end": v(330.77, -5713.2) * mm});
            skLineSegment(sketch, "E99.left", {"start": v(2190.77, -4663.2) * mm, "end": v(2190.77, -5713.2) * mm});
            skLineSegment(sketch, "E99.right", {"start": v(330.77, -4663.2) * mm, "end": v(330.77, -5713.2) * mm});
            skSolve(sketch);
        }
        {
            var Q0;
            Q0 = qSketchRegion(id + "F26", true);
            extrude(context, id + "F27", {"entities" : qUnion([Q0]), "operationType" : NewBodyOperationType.ADD, "depth" : 200 * mm, "offsetDistance" : 25 * mm});
        }
        {
            var Q0;
            {var subQ0=sQuery(id+"F9.wireOp",EDGE,"E68");var subQ1=sQuery(id+"F9.wireOp",EDGE,"E67");var subQ2=sQuery(id+"F9.wireOp",EDGE,"E66.top");var subQ3=sQuery(id+"F0.wireOp",EDGE,"E35");var subQ4=sQuery(id+"F9.wireOp",EDGE,"E69");var subQ5=sQuery(id+"F9.wireOp",EDGE,"E66.bottom");Q0=makeQuery(id+"F12.boolean.opBoolean","SPLIT",FACE,{"disambiguationData":[TD([makeQuery(id+"F1.opExtrude","SWEPT_FACE",FACE,{"disambiguationData":[OSD([subQ3])]})])],"derivedFrom":makeQuery(id+"F10.opExtrude","CAP_FACE",FACE,{"disambiguationData":[OSD([subQ5,subQ2,sQuery(id+"F9.wireOp",EDGE,"E66.right"),subQ1,subQ0,subQ4])],"isStart":true})});}
            var sketch = newSketch(context, id + "F28", { "sketchPlane" : qUnion([Q0])});
            skLineSegment(sketch, "E100", {"start": v(-2329.23, -5713.2) * mm, "end": v(-1049.23, -5713.2) * mm});
            skLineSegment(sketch, "E101", {"start": v(-1049.23, -5713.2) * mm, "end": v(230.77, -5713.2) * mm});
            skLineSegment(sketch, "E102", {"start": v(230.77, -5713.2) * mm, "end": v(230.77, -5113.2) * mm});
            skLineSegment(sketch, "E103", {"start": v(230.77, -5113.2) * mm, "end": v(-369.23, -5113.2) * mm, "construction": true});
            skLineSegment(sketch, "E104", {"start": v(-1049.23, -5113.2) * mm, "end": v(-1729.23, -5113.2) * mm});
            skLineSegment(sketch, "E105", {"start": v(-1729.23, -5113.2) * mm, "end": v(-1729.23, -5033.2) * mm});
            skLineSegment(sketch, "E106", {"start": v(-2329.23, -5033.2) * mm, "end": v(-2329.23, -5713.2) * mm});
            skLineSegment(sketch, "E107.top", {"start": v(-2329.23, -4233.2) * mm, "end": v(-1729.23, -4233.2) * mm});
            skLineSegment(sketch, "E107.left", {"start": v(-2329.23, -5033.2) * mm, "end": v(-2329.23, -4233.2) * mm});
            skLineSegment(sketch, "E107.right", {"start": v(-1729.23, -5033.2) * mm, "end": v(-1729.23, -4233.2) * mm});
            skLineSegment(sketch, "E108", {"start": v(-1049.23, -5713.2) * mm, "end": v(-1049.23, -5113.2) * mm, "construction": true});
            skLineSegment(sketch, "E109", {"start": v(-2329.23, -5033.2) * mm, "end": v(-1729.23, -5033.2) * mm, "construction": true});
            skLineSegment(sketch, "E110", {"start": v(230.77, -5113.2) * mm, "end": v(230.77, -4233.2) * mm});
            skLineSegment(sketch, "E111", {"start": v(230.77, -4233.2) * mm, "end": v(-369.23, -4233.2) * mm});
            skLineSegment(sketch, "E112", {"start": v(-369.23, -4233.2) * mm, "end": v(-369.23, -5113.2) * mm});
            skLineSegment(sketch, "E113", {"start": v(-369.23, -5113.2) * mm, "end": v(-1049.23, -5113.2) * mm});
            skSolve(sketch);
        }
        {
            var Q0;
            Q0=makeQuery(id+"F28.imprint","IMPRINT",FACE,{"disambiguationData":[TD([[makeQuery(id+"F28.imprint","IMPRINT",EDGE,{"derivedFrom":sQuery(id+"F28.wireOp",EDGE,"E100")}),1.0]])]});
            extrude(context, id + "F29", {"entities" : qUnion([Q0]), "operationType" : NewBodyOperationType.ADD, "depth" : 100 * mm, "offsetDistance" : 25 * mm});
        }
        {
            var Q0;
            Q0=makeQuery(id+"F29.opExtrude","CAP_FACE",FACE,{"disambiguationData":[OSD([sQuery(id+"F28.wireOp",EDGE,"E100"),sQuery(id+"F28.wireOp",EDGE,"E101"),sQuery(id+"F28.wireOp",EDGE,"E102"),sQuery(id+"F28.wireOp",EDGE,"E104"),sQuery(id+"F28.wireOp",EDGE,"E105"),sQuery(id+"F28.wireOp",EDGE,"E106"),sQuery(id+"F28.wireOp",EDGE,"E107.top"),sQuery(id+"F28.wireOp",EDGE,"E107.left"),sQuery(id+"F28.wireOp",EDGE,"E107.right"),sQuery(id+"F28.wireOp",EDGE,"E110"),sQuery(id+"F28.wireOp",EDGE,"E111"),sQuery(id+"F28.wireOp",EDGE,"E112"),sQuery(id+"F28.wireOp",EDGE,"E113")])],"isStart":false});
            var sketch = newSketch(context, id + "F30", { "sketchPlane" : qUnion([Q0])});
            skLineSegment(sketch, "E114", {"start": v(-2329.23, -4233.2) * mm, "end": v(-1729.23, -4233.2) * mm});
            skLineSegment(sketch, "E115", {"start": v(-1729.23, -4233.2) * mm, "end": v(-1729.23, -5113.2) * mm});
            skLineSegment(sketch, "E116", {"start": v(-1729.23, -5113.2) * mm, "end": v(-369.23, -5113.2) * mm});
            skLineSegment(sketch, "E117", {"start": v(-369.23, -5113.2) * mm, "end": v(-369.23, -4233.2) * mm});
            skLineSegment(sketch, "E118", {"start": v(-369.23, -4233.2) * mm, "end": v(230.77, -4233.2) * mm});
            skLineSegment(sketch, "E119", {"start": v(230.77, -4233.2) * mm, "end": v(230.77, -5713.2) * mm});
            skLineSegment(sketch, "E120", {"start": v(230.77, -5713.2) * mm, "end": v(-2329.23, -5713.2) * mm});
            skLineSegment(sketch, "E121", {"start": v(-2329.23, -5713.2) * mm, "end": v(-2329.23, -4233.2) * mm});
            skSolve(sketch);
        }
        {
            var Q0;
            Q0 = qSketchRegion(id + "F30", true);
            extrude(context, id + "F31", {"entities" : qUnion([Q0]), "depth" : 850 * mm, "offsetDistance" : 25 * mm});
        }
        {
            var Q0;
            Q0=makeQuery(id+"F15.opExtrude","SWEPT_FACE",FACE,{"disambiguationData":[OSD([sQuery(id+"F14.wireOp",EDGE,"E73.top")])]});
            var sketch = newSketch(context, id + "F32", { "sketchPlane" : qUnion([Q0])});
            skLineSegment(sketch, "E122.bottom", {"start": v(-851.06, 2090) * mm, "end": v(-247.06, 2090) * mm});
            skLineSegment(sketch, "E122.top", {"start": v(-851.06, 1886) * mm, "end": v(-247.06, 1886) * mm});
            skLineSegment(sketch, "E122.left", {"start": v(-851.06, 2090) * mm, "end": v(-851.06, 1886) * mm});
            skLineSegment(sketch, "E122.right", {"start": v(-247.06, 2090) * mm, "end": v(-247.06, 1886) * mm});
            skSolve(sketch);
        }
        {
            var Q0;
            Q0 = qSketchRegion(id + "F32", true);
            extrude(context, id + "F33", {"entities" : qUnion([Q0]), "oppositeDirection" : true, "depth" : 300 * mm, "offsetDistance" : 25 * mm});
        }
        {
            var Q0;
            Q0=makeQuery(id+"F17.boolean.opBoolean","MERGE",FACE,{"derivedFrom":[makeQuery(id+"F15.opExtrude","SWEPT_FACE",FACE,{"disambiguationData":[OSD([sQuery(id+"F14.wireOp",EDGE,"E75.right")])]}),makeQuery(id+"F17.opExtrude","CAP_FACE",FACE,{"disambiguationData":[OSD([sQuery(id+"F16.wireOp",EDGE,"E80"),sQuery(id+"F16.wireOp",EDGE,"E81"),sQuery(id+"F16.wireOp",EDGE,"E82"),sQuery(id+"F16.wireOp",EDGE,"E83"),sQuery(id+"F16.wireOp",EDGE,"E84"),sQuery(id+"F16.wireOp",EDGE,"E85"),sQuery(id+"F16.wireOp",EDGE,"E86"),sQuery(id+"F16.wireOp",EDGE,"E87"),sQuery(id+"F16.wireOp",EDGE,"E88"),sQuery(id+"F16.wireOp",EDGE,"E89"),sQuery(id+"F16.wireOp",EDGE,"E90"),sQuery(id+"F16.wireOp",EDGE,"E91"),sQuery(id+"F16.wireOp",EDGE,"E92"),sQuery(id+"F16.wireOp",EDGE,"E93")])],"isStart":true})]});
            var sketch = newSketch(context, id + "F34", { "sketchPlane" : qUnion([Q0])});
            skLineSegment(sketch, "E123.bottom", {"start": v(-5519, 2090) * mm, "end": v(-4915, 2090) * mm});
            skLineSegment(sketch, "E123.top", {"start": v(-5519, 1886) * mm, "end": v(-4915, 1886) * mm});
            skLineSegment(sketch, "E123.left", {"start": v(-5519, 2090) * mm, "end": v(-5519, 1886) * mm});
            skLineSegment(sketch, "E123.right", {"start": v(-4915, 2090) * mm, "end": v(-4915, 1886) * mm});
            skSolve(sketch);
        }
        {
            var Q0;
            Q0 = qSketchRegion(id + "F34", true);
            extrude(context, id + "F35", {"entities" : qUnion([Q0]), "oppositeDirection" : true, "depth" : 300 * mm, "offsetDistance" : 25 * mm});
        }
        {
            var Q0;
            Q0=makeQuery(id+"F15.opExtrude","SWEPT_FACE",FACE,{"disambiguationData":[OSD([sQuery(id+"F14.wireOp",EDGE,"E72.left")])]});
            var sketch = newSketch(context, id + "F36", { "sketchPlane" : qUnion([Q0])});
            skLineSegment(sketch, "E124.bottom", {"start": v(3422.2, 1837.17) * mm, "end": v(4026.2, 1837.17) * mm});
            skLineSegment(sketch, "E124.top", {"start": v(3422.2, 1633.17) * mm, "end": v(4026.2, 1633.17) * mm});
            skLineSegment(sketch, "E124.left", {"start": v(3422.2, 1837.17) * mm, "end": v(3422.2, 1633.17) * mm});
            skLineSegment(sketch, "E124.right", {"start": v(4026.2, 1837.17) * mm, "end": v(4026.2, 1633.17) * mm});
            skSolve(sketch);
        }
        {
            var Q0;
            Q0 = qSketchRegion(id + "F36", true);
            extrude(context, id + "F37", {"entities" : qUnion([Q0]), "oppositeDirection" : true, "depth" : 300 * mm, "offsetDistance" : 25 * mm});
        }
    });
